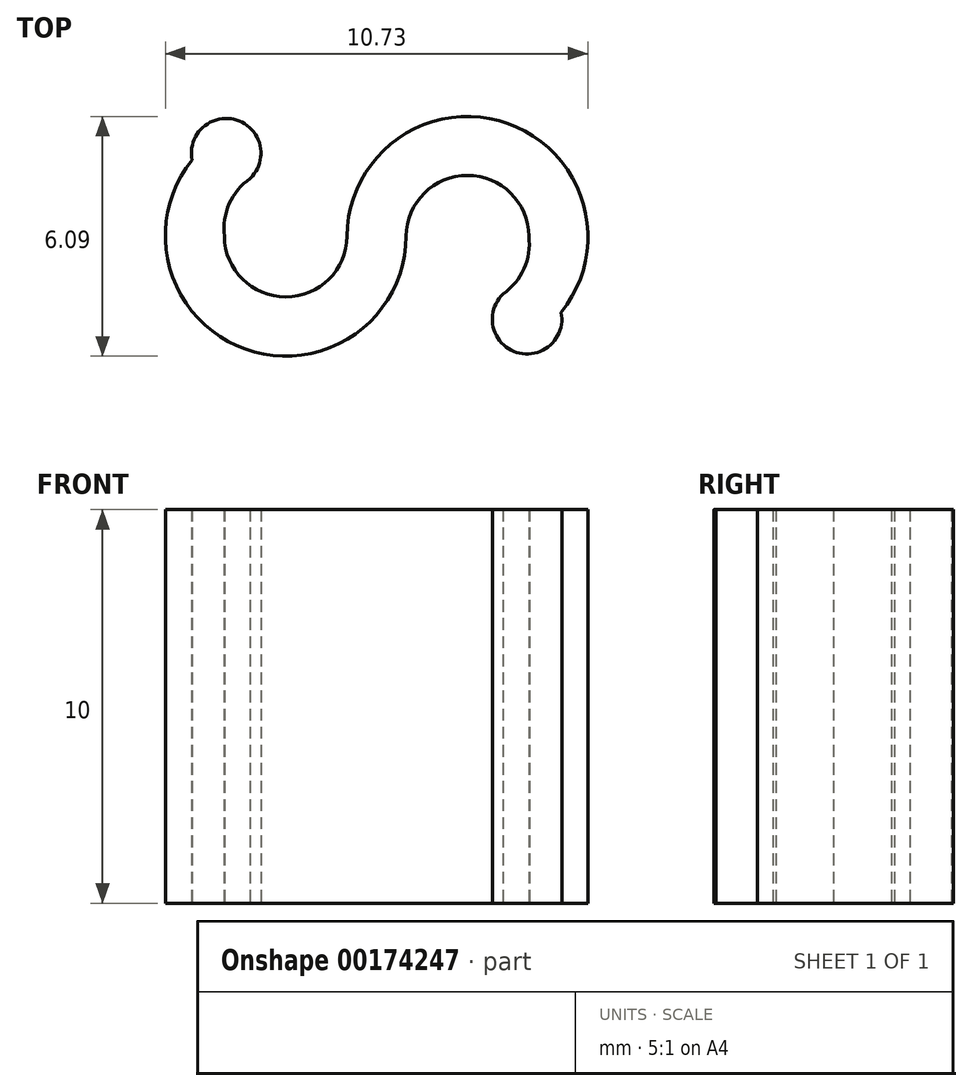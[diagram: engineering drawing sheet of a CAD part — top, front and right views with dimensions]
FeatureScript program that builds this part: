
annotation { "Feature Type Name" : "Feature", "Feature Type Description" : "" }
export const myFeature = defineFeature(function(context is Context, id is Id, definition is map)
    precondition{}
    {
        {
            var Q0;
            Q0=qCreatedBy(makeId("Top.planeOp"),FACE);
            var sketch = newSketch(context, id + "F0", { "sketchPlane" : qUnion([Q0])});
            skArc(sketch, "E0", {"start": v(-33.2, 19.28) * mm, "mid": v(-34.77, 20.83) * mm, "end": v(-36.33, 19.28) * mm});
            skPoint(sketch, "E1.endSnap0", {"position": v(-34.77, 20.83) * mm});
            skArc(sketch, "E2", {"start": v(-33.86, 17.82) * mm, "mid": v(-33.33, 18.46) * mm, "end": v(-33.2, 19.28) * mm});
            skArc(sketch, "E3", {"start": v(-33.86, 17.82) * mm, "mid": v(-33.52, 16.33) * mm, "end": v(-32.39, 17.35) * mm});
            skArc(sketch, "E4", {"start": v(-32.39, 17.35) * mm, "mid": v(-32.12, 20.8) * mm, "end": v(-35.25, 22.3) * mm});
            skArc(sketch, "E5", {"start": v(-35.25, 22.3) * mm, "mid": v(-37.09, 21.26) * mm, "end": v(-37.83, 19.28) * mm});
            skPoint(sketch, "E6.startSnap0", {"position": v(-37.08, 19.28) * mm});
            skLineSegment(sketch, "E7", {"start": v(-37.83, 19.28) * mm, "end": v(-36.33, 19.28) * mm});
            skArc(sketch, "E8.MirrorCS", {"start": v(-40.29, 20.75) * mm, "mid": v(-40.63, 22.24) * mm, "end": v(-41.77, 21.22) * mm});
            skArc(sketch, "E9.MirrorCS", {"start": v(-38.9, 16.28) * mm, "mid": v(-37.06, 17.3) * mm, "end": v(-36.33, 19.28) * mm});
            skArc(sketch, "E10.MirrorCS", {"start": v(-41.77, 21.22) * mm, "mid": v(-42.03, 17.76) * mm, "end": v(-38.9, 16.28) * mm});
            skArc(sketch, "E11.MirrorCS", {"start": v(-40.29, 20.75) * mm, "mid": v(-40.82, 20.1) * mm, "end": v(-40.94, 19.28) * mm});
            skArc(sketch, "E12.MirrorCS", {"start": v(-40.94, 19.28) * mm, "mid": v(-39.38, 17.74) * mm, "end": v(-37.83, 19.28) * mm});
            skSolve(sketch);
        }
        {
            var Q0;
            Q0=makeQuery(id+"F0.imprint","IMPRINT",FACE,{"disambiguationData":[TD([[makeQuery(id+"F0.imprint","IMPRINT",EDGE,{"derivedFrom":sQuery(id+"F0.wireOp",EDGE,"E7")}),-1.0]])]});
            var Q1;
            Q1=makeQuery(id+"F0.imprint","IMPRINT",FACE,{"disambiguationData":[TD([[makeQuery(id+"F0.imprint","IMPRINT",EDGE,{"derivedFrom":sQuery(id+"F0.wireOp",EDGE,"E0")}),-1.0]])]});
            extrude(context, id + "F1", {"entities" : qUnion([Q0, Q1]), "depth" : 10 * mm});
        }
    });
